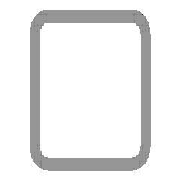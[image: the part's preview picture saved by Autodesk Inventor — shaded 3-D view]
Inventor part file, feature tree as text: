
AUTODESK INVENTOR PART (.ipt)
format: ipt  version: 2025 (Build 290162010, 162A)  size: 135,168 bytes
history: native  units: mm (DEFAULTED — no unit token found)
features: other x4, sketch x1, plane x1
ambient origin geometry x8: Origin, YZ Plane, XZ Plane, XY Plane, X Axis, Y Axis, Z Axis, Center Point
bodies: Solid1 (feature_tree), Body (feature_tree)
feature tree (6):
  parser-record x1  (decoder bookkeeping rows leaked as tree rows — omitted from the tree; the rows remain in map.json)
  other  "Driven Length"
  other  "Start Plane"
  other  "End Plane"
  sketch  "Sketch3"  dims[d3=1420.0mm d4=0.0mm d7=4.0mm d9=40.0mm d11=40.0mm d12=2.0mm d13=40.0mm d14=1460.0mm d15=20.0mm d16=20.0mm d17=90.0deg d18=1420.0mm]
  plane  "Work Plane3"
